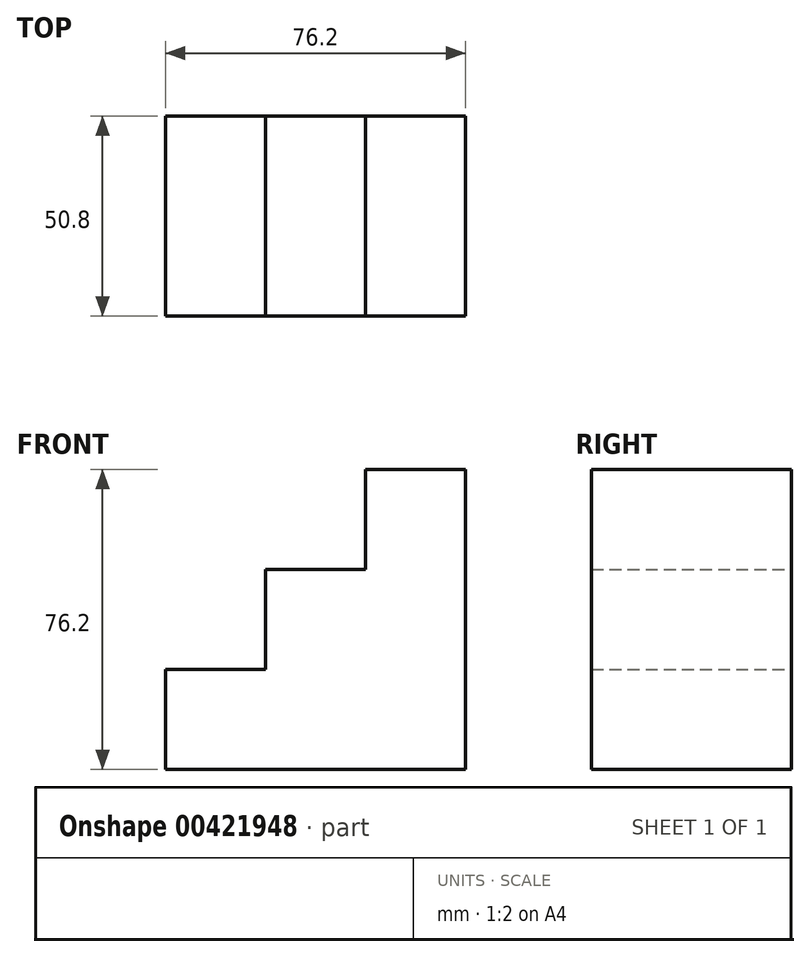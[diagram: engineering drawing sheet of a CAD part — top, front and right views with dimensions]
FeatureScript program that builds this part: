
annotation { "Feature Type Name" : "Feature", "Feature Type Description" : "" }
export const myFeature = defineFeature(function(context is Context, id is Id, definition is map)
    precondition{}
    {
        {
            var Q0;
            Q0=qCreatedBy(makeId("Front.planeOp"),FACE);
            var sketch = newSketch(context, id + "F0", { "sketchPlane" : qUnion([Q0])});
            skLineSegment(sketch, "E0", {"start": v(-76.2, 0) * mm, "end": v(0, 0) * mm});
            skLineSegment(sketch, "E1", {"start": v(0, 0) * mm, "end": v(0, 76.2) * mm});
            skLineSegment(sketch, "E2", {"start": v(0, 76.2) * mm, "end": v(-25.4, 76.2) * mm});
            skLineSegment(sketch, "E3", {"start": v(-25.4, 76.2) * mm, "end": v(-25.4, 50.8) * mm});
            skLineSegment(sketch, "E4", {"start": v(-25.4, 50.8) * mm, "end": v(-50.8, 50.8) * mm});
            skLineSegment(sketch, "E5", {"start": v(-50.8, 50.8) * mm, "end": v(-50.8, 25.4) * mm});
            skLineSegment(sketch, "E6", {"start": v(-50.8, 25.4) * mm, "end": v(-76.2, 25.4) * mm});
            skLineSegment(sketch, "E7", {"start": v(-76.2, 25.4) * mm, "end": v(-76.2, 0) * mm});
            skSolve(sketch);
        }
        {
            var Q0;
            Q0 = qSketchRegion(id + "F0", true);
            extrude(context, id + "F1", {"entities" : qUnion([Q0]), "depth" : 50.8 * mm});
        }
    });
